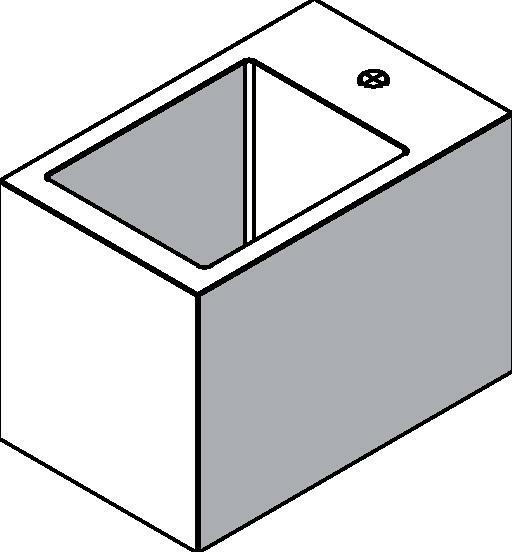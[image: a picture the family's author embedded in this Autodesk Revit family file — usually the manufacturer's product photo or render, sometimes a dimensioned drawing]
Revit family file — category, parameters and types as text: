
# Revit family: Deca_Cuba suspensa retangular multi uso com mesa_Cubas Espec._L.116D
name_source: partatom
category: Plumbing Fixtures
units: mm (PartAtom-declared; Revit-internal decimal feet)

## family parameters
Cut with Voids When Loaded = No
Host = Face
Part Type = Normal
Room Calculation Point = No
Round Connector Dimension = Use Radius
Shared = No

## types (2) — shared parameters
Acompanha o Produto = Parafusos de fixação e esfregador de madeira
Aprovado por = quattroD
Atendimento ao Cliente = 0800-0117073
Categoria = CUBAS
Composição Anel Vedação = -
Composição Assento = -
Composição Básica = Argila, feldspato, caulim, vidrados e corantes inorgânicos e madeira.
Composição Componente = Não Possui
Consumo = -
Cor Interna = -
Cor Secundária = -
Cores Componente = Não Possui
Criado por = quattroD
Código Pai = L.116D
Default Elevation = 900 mm  [stored 2.95276 ft]
Description = Cuba suspensa retangular multi uso com mesa
Diâmetro Ponto de Esgoto = 25 mm  [stored 0.082021 ft]
Informações Complementares = -
Itens de Instalação = 1606.C.DUO; 1680.C.114
Linha = Cubas Espec.
Manufacturer = Deca
Norma = NBR-16728-1;NBR-16728-2
Peso Líquido (Kg) = 37.504
Pressão máx. funcionamento = -
Pressão mín. Aquec. Acúmulo = -
Pressão mín. Aquec. Passagem = -
Pressão mín. funcionamento = -
Raio Ponto de Esgoto = 13 mm
Saída de Esgoto = Válvula Longa
Segmento = Banheiro Luxo
Tipo de dispositivo economizador = -
Tipo de mecanismo utilizado = -
Tipo de rosca de entrada = -
Tipo de rosca de saída = -
URL = www.deca.com.br
Vazão na Pressão máx. (L/min) = -
Vazão na Pressão mín. (L/min) = -
zero-valued in all types: WFU

## per-type parameters (varying)
| type | Cor Principal | Material | Model |
| L.116D.17_Branco | Branco | Deca_Branco | L.116D.17 |
| L.116D.95_Ébano | Ébano | Deca_Ébano | L.116D.95 |

note: [stored X ft] marks values corroborated as IEEE doubles in the binary element streams (Revit-internal decimal feet)

## geometry (parser evidence)
native form markers: Sweep x2
no freeform markers — native parametric forms only
